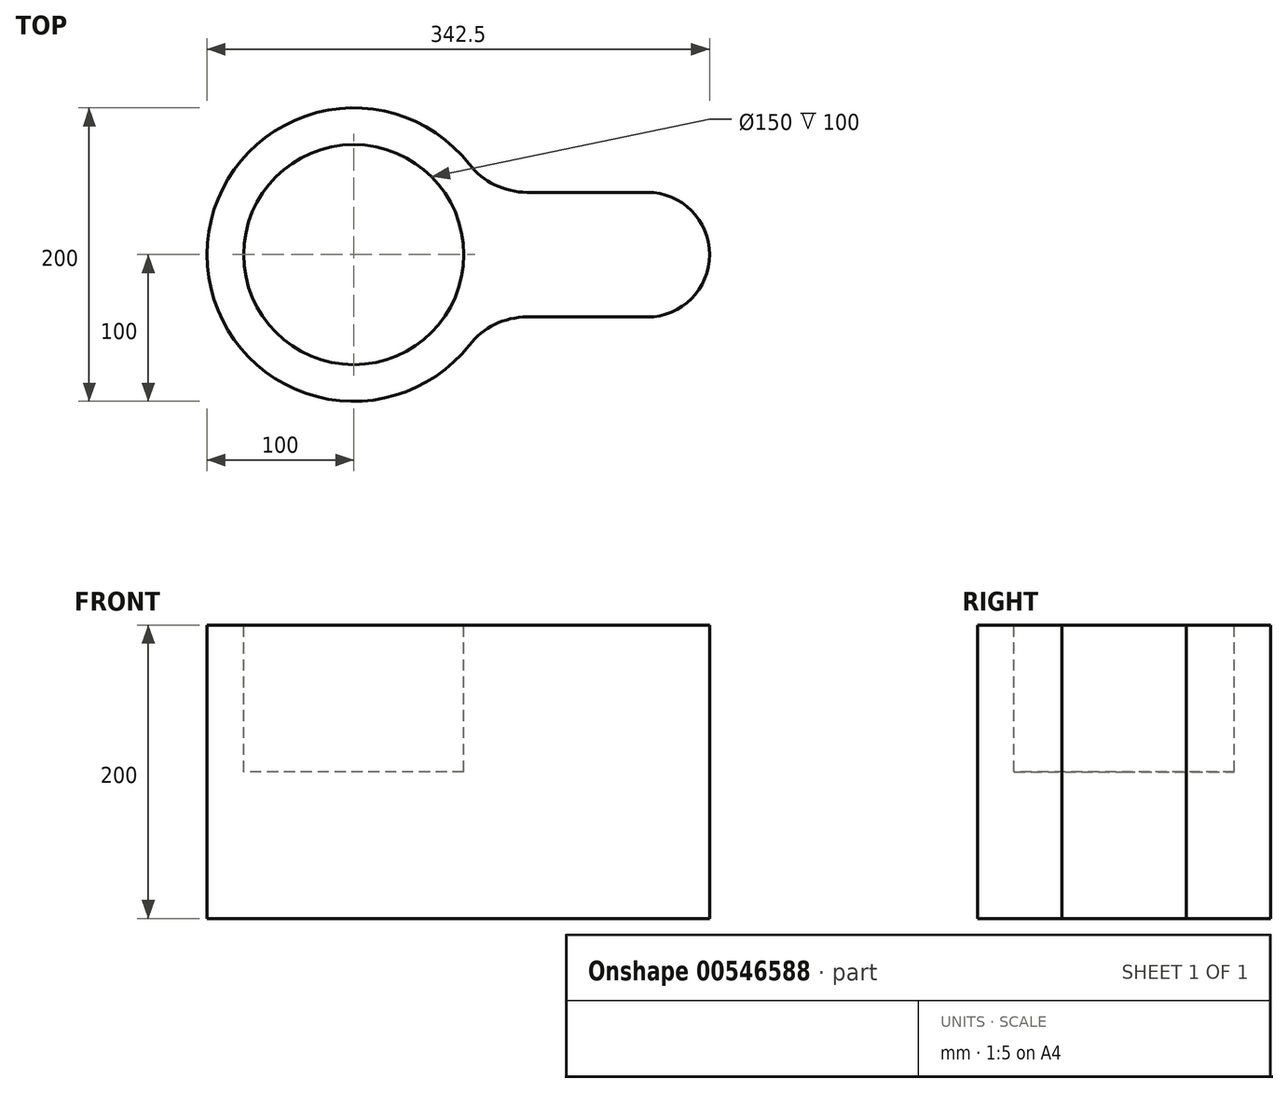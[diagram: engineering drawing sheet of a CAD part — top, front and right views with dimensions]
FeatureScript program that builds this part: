
annotation { "Feature Type Name" : "Feature", "Feature Type Description" : "" }
export const myFeature = defineFeature(function(context is Context, id is Id, definition is map)
    precondition{}
    {
        {
            var Q0;
            Q0=qCreatedBy(makeId("Top.planeOp"),FACE);
            var sketch = newSketch(context, id + "F0", { "sketchPlane" : qUnion([Q0])});
            skArc(sketch, "E0", {"start": v(78.72, 61.67) * mm, "mid": v(-100, 0) * mm, "end": v(78.72, -61.67) * mm});
            skArc(sketch, "E1", {"start": v(200, -42.5) * mm, "mid": v(242.5, 0) * mm, "end": v(200, 42.5) * mm});
            skLineSegment(sketch, "E2", {"start": v(0, 0) * mm, "end": v(200, 0) * mm, "construction": true});
            skLineSegment(sketch, "E3", {"start": v(118.08, 42.5) * mm, "end": v(200, 42.5) * mm});
            skLineSegment(sketch, "E4", {"start": v(118.08, -42.5) * mm, "end": v(200, -42.5) * mm});
            skPoint(sketch, "E5.visualSharp", {"position": v(90.52, 42.5) * mm});
            skArc(sketch, "E5.filletArc", {"start": v(78.72, 61.67) * mm, "mid": v(96.2, 47.55) * mm, "end": v(118.08, 42.5) * mm});
            skPoint(sketch, "E6.visualSharp", {"position": v(90.52, -42.5) * mm});
            skArc(sketch, "E6.filletArc", {"start": v(118.08, -42.5) * mm, "mid": v(96.2, -47.55) * mm, "end": v(78.72, -61.67) * mm});
            skSolve(sketch);
        }
        {
            var Q0;
            Q0=makeQuery(id+"F0.imprint","IMPRINT",FACE,{"disambiguationData":[TD([[makeQuery(id+"F0.imprint","IMPRINT",EDGE,{"derivedFrom":sQuery(id+"F0.wireOp",EDGE,"E0")}),1.0]])]});
            var sketch = newSketch(context, id + "F1", { "sketchPlane" : qUnion([Q0])});
            skSolve(sketch);
        }
        {
            var Q0;
            Q0=makeQuery(id+"F1.imprint","IMPRINT",FACE,{"disambiguationData":[TD([[makeQuery(id+"F1.imprint","IMPRINT",EDGE,{"derivedFrom":makeQuery(id+"F0.imprint","IMPRINT",EDGE,{"derivedFrom":sQuery(id+"F0.wireOp",EDGE,"E0")})}),1.0]])]});
            var Q1;
            Q1=makeQuery(id+"F0.imprint","IMPRINT",FACE,{"disambiguationData":[TD([[makeQuery(id+"F0.imprint","IMPRINT",EDGE,{"derivedFrom":sQuery(id+"F0.wireOp",EDGE,"E0")}),1.0]])]});
            extrude(context, id + "F2", {"entities" : qUnion([Q0, Q1]), "depth" : 200 * mm, "offsetDistance" : 25 * mm});
        }
        {
            var Q0;
            {var subQ0=sQuery(id+"F0.wireOp",EDGE,"E6.filletArc");var subQ1=sQuery(id+"F0.wireOp",EDGE,"E5.filletArc");var subQ2=sQuery(id+"F0.wireOp",EDGE,"E4");var subQ3=sQuery(id+"F0.wireOp",EDGE,"E3");var subQ4=sQuery(id+"F0.wireOp",EDGE,"E1");var subQ5=sQuery(id+"F0.wireOp",EDGE,"E0");Q0=makeQuery(id+"F2.opExtrude","CAP_FACE",FACE,{"disambiguationData":[OSD([subQ5,subQ4,subQ3,subQ2,subQ1,subQ0]),TDD([makeQuery(id+"F1.imprint","IMPRINT",EDGE,{"derivedFrom":makeQuery(id+"F0.imprint","IMPRINT",EDGE,{"derivedFrom":subQ5})}),makeQuery(id+"F1.imprint","IMPRINT",EDGE,{"derivedFrom":makeQuery(id+"F0.imprint","IMPRINT",EDGE,{"derivedFrom":subQ4})}),makeQuery(id+"F1.imprint","IMPRINT",EDGE,{"derivedFrom":makeQuery(id+"F0.imprint","IMPRINT",EDGE,{"derivedFrom":subQ3})}),makeQuery(id+"F1.imprint","IMPRINT",EDGE,{"derivedFrom":makeQuery(id+"F0.imprint","IMPRINT",EDGE,{"derivedFrom":subQ2})}),makeQuery(id+"F1.imprint","IMPRINT",EDGE,{"derivedFrom":makeQuery(id+"F0.imprint","IMPRINT",EDGE,{"derivedFrom":subQ1})}),makeQuery(id+"F1.imprint","IMPRINT",EDGE,{"derivedFrom":makeQuery(id+"F0.imprint","IMPRINT",EDGE,{"derivedFrom":subQ0})})])],"isStart":false});}
            var sketch = newSketch(context, id + "F3", { "sketchPlane" : qUnion([Q0])});
            skCircle(sketch, "E7", {"center": v(0, 0) * mm, "radius": 75 * mm});
            skSolve(sketch);
        }
        {
            var Q0;
            Q0=makeQuery(id+"F3.imprint","IMPRINT",FACE,{"disambiguationData":[TD([[makeQuery(id+"F3.imprint","IMPRINT",EDGE,{"derivedFrom":sQuery(id+"F3.wireOp",EDGE,"E7")}),1.0]])]});
            extrude(context, id + "F4", {"entities" : qUnion([Q0]), "operationType" : NewBodyOperationType.REMOVE, "oppositeDirection" : true, "depth" : 100 * mm, "offsetDistance" : 25 * mm});
        }
    });
